# Revit family: MBA_Штора_ДымозащитнаяРулонная_FireTechnics_ПротиводымнаяE60
name_source: partatom
category: Двери
revit_build: Autodesk Revit 2016 (Build: 20160314_0715(x64)
units: mm (PartAtom-declared; Revit-internal decimal feet)

## family parameters
Всегда вертикально = Да
Заголовок OmniClass = Rolling Fire Doors
Номер OmniClass = 23.30.10.21.11.11
Общий = Нет
Основа = Стена
При загрузке вырезать с полостями = Нет
Точка расчета площади = Нет

## types (1)
- 3000х3000
    ADSK_URL страницы изделия = https://mva-rolltor.ru
    ADSK_Единица измерения = шт.
    ADSK_Завод-изготовитель = МВА
    ADSK_Масса_Текст = Вес полотна: 435 г/м2
    ADSK_Наименование = Противопожарная дымозащитная штора рулонная E60 (противодымная) без орошения водой 3000х3000
    ADSK_Наименование краткое = Противопожарная дымозащитная штора рулонная 3000х3000
    ADSK_Обозначение = ТУ 5284-001-16123348-2020
    ADSK_Предел огнестойкости = E60
    ADSK_Размер_Высота = 3000 мм
    ADSK_Размер_Ширина = 3000 мм
    URL = https://mva-rolltor.ru
    Аналитическая конструкция = <Нет>
    Высота = 3150 мм
    Высота короба = 150 мм
    Высота направляющих = 80 мм
    Замыкание стены = По основе
    Изготовитель = МВА
    Максимальная высота проема = 6000 мм
    Максимальная ширина проема = 6500 мм
    Материал направляющих = Сталь_оцинкованная_листовая МВА
    Материал полотна = Firetex™ 600
    Минимальная высота проема = 1000 мм
    Минимальная ширина проема = 1000 мм
    Огнестойкость = E60
    Описание = Противодымные автоматические шторы типа FireTechnics E60 (без орошения водой) предотвращают распространения задымления и отводят дым к системам дымоудаления, предоставляя возможность проведения безопасной эвакуации людей и спасения материальных ценностей от воздействия продуктов горения.
    Примерная высота = 3000 мм
    Примерная ширина = 3000 мм
    Тип конструкций = Штора дымозащитная
    Толщина = 10 мм
    Функция = Внутренние слои
    Ширина = 3120 мм
    Ширина короба = 150 мм
    Ширина направляющих = 60 мм
